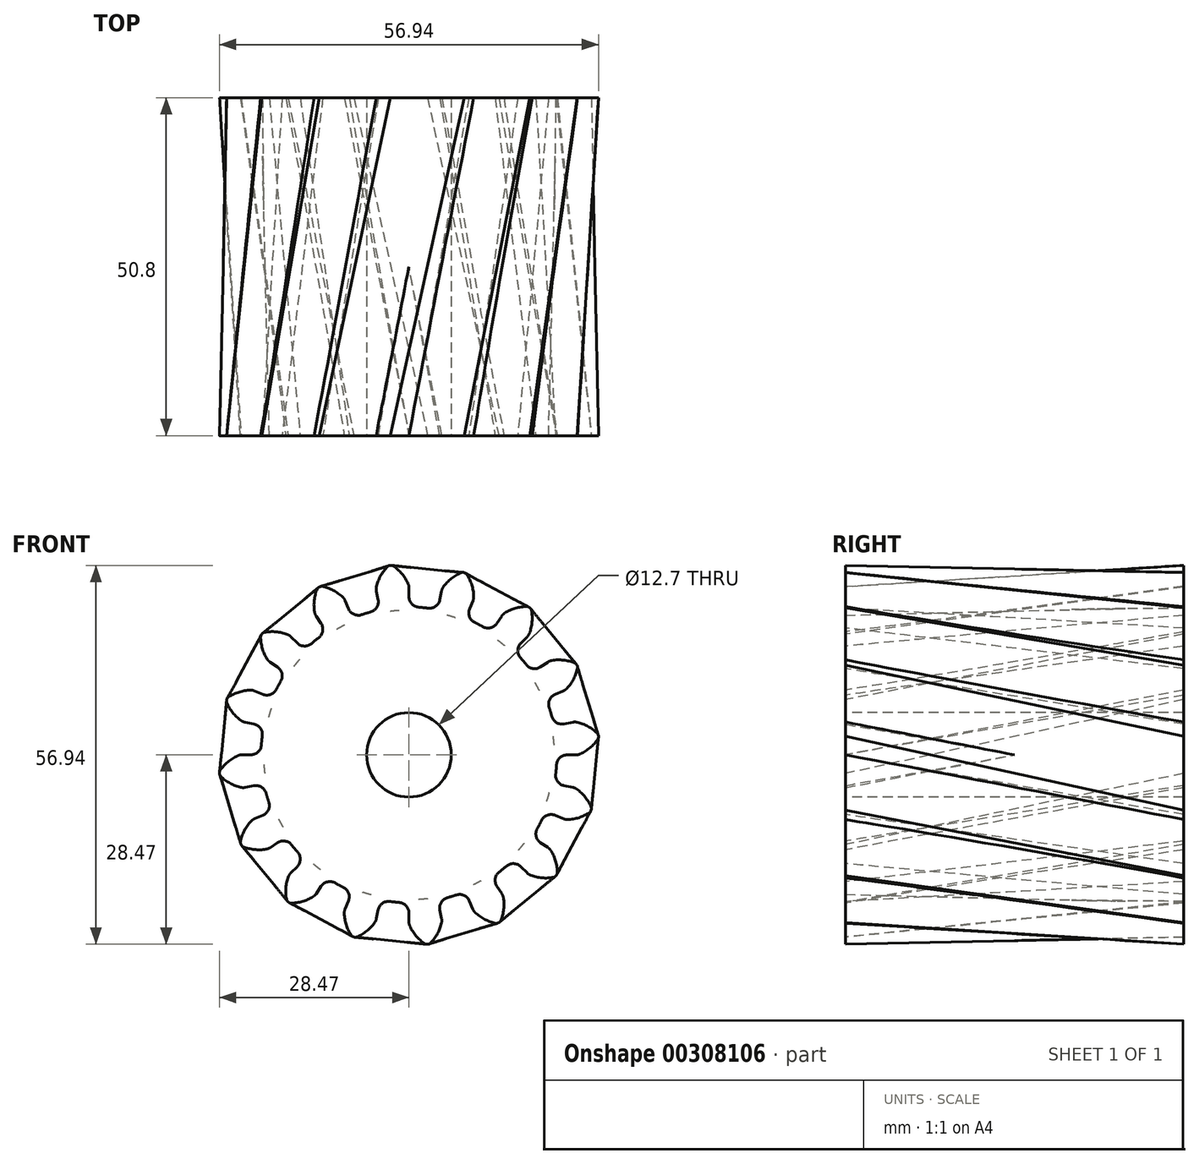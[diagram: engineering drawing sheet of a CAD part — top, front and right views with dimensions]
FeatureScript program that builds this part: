
annotation { "Feature Type Name" : "Feature", "Feature Type Description" : "" }
export const myFeature = defineFeature(function(context is Context, id is Id, definition is map)
    precondition{}
    {
        {
            var Q0;
            Q0=qCreatedBy(makeId("Front.planeOp"),FACE);
            var sketch = newSketch(context, id + "F0", { "sketchPlane" : qUnion([Q0])});
            skArc(sketch, "E0", {"start": v(-5.78, 21.46) * mm, "mid": v(-6.45, 21.27) * mm, "end": v(-7.11, 21.06) * mm});
            skArc(sketch, "E1.trimOffspring", {"start": v(-0.14, 25.74) * mm, "mid": v(-1.06, 27.21) * mm, "end": v(-2.36, 28.38) * mm});
            skLineSegment(sketch, "E2", {"start": v(-2.64, 28.47) * mm, "end": v(-2.8, 28.47) * mm});
            skLineSegment(sketch, "E3", {"start": v(0, 25.08) * mm, "end": v(0, 23.76) * mm});
            skLineSegment(sketch, "E4.MirrorCS", {"start": v(-2.96, 28.44) * mm, "end": v(-2.8, 28.47) * mm});
            skArc(sketch, "E5.MirrorCS", {"start": v(-4.89, 25.27) * mm, "mid": v(-4.27, 26.9) * mm, "end": v(-3.22, 28.3) * mm});
            skLineSegment(sketch, "E6.MirrorCS", {"start": v(-4.9, 24.6) * mm, "end": v(-4.64, 23.3) * mm});
            skPoint(sketch, "E7.orphan", {"position": v(-4.19, 21.03) * mm});
            skPoint(sketch, "E8.orphan", {"position": v(0, 21.44) * mm});
            skPoint(sketch, "E9.visualSharp", {"position": v(-3.1, 28.4) * mm});
            skArc(sketch, "E9.filletArc", {"start": v(-2.96, 28.44) * mm, "mid": v(-3.1, 28.38) * mm, "end": v(-3.22, 28.3) * mm});
            skPoint(sketch, "E10.visualSharp", {"position": v(-2.5, 28.47) * mm});
            skArc(sketch, "E10.filletArc", {"start": v(-2.36, 28.38) * mm, "mid": v(-2.5, 28.44) * mm, "end": v(-2.64, 28.47) * mm});
            skPoint(sketch, "E11.visualSharp", {"position": v(-4.96, 24.91) * mm});
            skArc(sketch, "E11.filletArc", {"start": v(-4.89, 25.27) * mm, "mid": v(-4.93, 24.94) * mm, "end": v(-4.9, 24.6) * mm});
            skPoint(sketch, "E12.visualSharp", {"position": v(0, 25.4) * mm});
            skArc(sketch, "E12.filletArc", {"start": v(0, 25.08) * mm, "mid": v(-0.03, 25.42) * mm, "end": v(-0.14, 25.74) * mm});
            skPoint(sketch, "E13.visualSharp", {"position": v(-4.34, 21.8) * mm});
            skArc(sketch, "E13.filletArc", {"start": v(-5.78, 21.46) * mm, "mid": v(-4.85, 22.15) * mm, "end": v(-4.64, 23.3) * mm});
            skPoint(sketch, "E14.visualSharp", {"position": v(0, 22.22) * mm});
            skArc(sketch, "E14.filletArc", {"start": v(0, 23.76) * mm, "mid": v(0.43, 22.67) * mm, "end": v(1.49, 22.18) * mm});
            skArc(sketch, "E15.1.0", {"start": v(-13.56, 17.61) * mm, "mid": v(-12.96, 18.61) * mm, "end": v(-13.2, 19.75) * mm});
            skLineSegment(sketch, "E15.1.1", {"start": v(-13.94, 20.85) * mm, "end": v(-13.2, 19.75) * mm});
            skArc(sketch, "E15.1.2", {"start": v(-14.19, 21.47) * mm, "mid": v(-14.1, 21.15) * mm, "end": v(-13.94, 20.85) * mm});
            skArc(sketch, "E15.1.3", {"start": v(-14.19, 21.47) * mm, "mid": v(-14.23, 23.22) * mm, "end": v(-13.8, 24.9) * mm});
            skArc(sketch, "E15.1.4", {"start": v(-13.62, 25.14) * mm, "mid": v(-13.73, 25.04) * mm, "end": v(-13.8, 24.9) * mm});
            skLineSegment(sketch, "E15.1.5", {"start": v(-13.62, 25.14) * mm, "end": v(-13.48, 25.23) * mm});
            skLineSegment(sketch, "E15.1.6", {"start": v(-13.34, 25.29) * mm, "end": v(-13.48, 25.23) * mm});
            skArc(sketch, "E15.1.7", {"start": v(-13.04, 25.32) * mm, "mid": v(-13.2, 25.32) * mm, "end": v(-13.34, 25.29) * mm});
            skArc(sketch, "E15.1.8", {"start": v(-9.97, 23.73) * mm, "mid": v(-11.4, 24.73) * mm, "end": v(-13.04, 25.32) * mm});
            skArc(sketch, "E15.1.9", {"start": v(-9.6, 23.18) * mm, "mid": v(-9.75, 23.47) * mm, "end": v(-9.97, 23.73) * mm});
            skLineSegment(sketch, "E15.1.10", {"start": v(-9.6, 23.18) * mm, "end": v(-9.09, 21.95) * mm});
            skArc(sketch, "E15.1.11", {"start": v(-9.09, 21.95) * mm, "mid": v(-8.28, 21.11) * mm, "end": v(-7.11, 21.06) * mm});
            skArc(sketch, "E15.2.0", {"start": v(-19.26, 11.08) * mm, "mid": v(-19.1, 12.24) * mm, "end": v(-19.76, 13.2) * mm});
            skLineSegment(sketch, "E15.2.1", {"start": v(-20.86, 13.93) * mm, "end": v(-19.76, 13.2) * mm});
            skArc(sketch, "E15.2.2", {"start": v(-21.32, 14.41) * mm, "mid": v(-21.12, 14.15) * mm, "end": v(-20.86, 13.93) * mm});
            skArc(sketch, "E15.2.3", {"start": v(-21.32, 14.41) * mm, "mid": v(-22.03, 16) * mm, "end": v(-22.29, 17.73) * mm});
            skArc(sketch, "E15.2.4", {"start": v(-22.2, 18.01) * mm, "mid": v(-22.26, 17.88) * mm, "end": v(-22.29, 17.73) * mm});
            skLineSegment(sketch, "E15.2.5", {"start": v(-22.2, 18.01) * mm, "end": v(-22.11, 18.15) * mm});
            skLineSegment(sketch, "E15.2.6", {"start": v(-22, 18.26) * mm, "end": v(-22.11, 18.15) * mm});
            skArc(sketch, "E15.2.7", {"start": v(-21.74, 18.4) * mm, "mid": v(-21.88, 18.35) * mm, "end": v(-22, 18.26) * mm});
            skArc(sketch, "E15.2.8", {"start": v(-18.3, 18.1) * mm, "mid": v(-20, 18.49) * mm, "end": v(-21.74, 18.4) * mm});
            skArc(sketch, "E15.2.9", {"start": v(-17.73, 17.74) * mm, "mid": v(-18, 17.95) * mm, "end": v(-18.3, 18.1) * mm});
            skLineSegment(sketch, "E15.2.10", {"start": v(-17.73, 17.74) * mm, "end": v(-16.8, 16.8) * mm});
            skArc(sketch, "E15.2.11", {"start": v(-16.8, 16.8) * mm, "mid": v(-15.73, 16.34) * mm, "end": v(-14.63, 16.73) * mm});
            skArc(sketch, "E15.3.0", {"start": v(-22.04, 2.87) * mm, "mid": v(-22.32, 4) * mm, "end": v(-23.3, 4.63) * mm});
            skLineSegment(sketch, "E15.3.1", {"start": v(-24.6, 4.89) * mm, "end": v(-23.3, 4.63) * mm});
            skArc(sketch, "E15.3.2", {"start": v(-25.22, 5.15) * mm, "mid": v(-24.92, 4.99) * mm, "end": v(-24.6, 4.89) * mm});
            skArc(sketch, "E15.3.3", {"start": v(-25.22, 5.15) * mm, "mid": v(-26.48, 6.35) * mm, "end": v(-27.37, 7.85) * mm});
            skArc(sketch, "E15.3.4", {"start": v(-27.4, 8.15) * mm, "mid": v(-27.41, 8) * mm, "end": v(-27.37, 7.85) * mm});
            skLineSegment(sketch, "E15.3.5", {"start": v(-27.4, 8.15) * mm, "end": v(-27.37, 8.3) * mm});
            skLineSegment(sketch, "E15.3.6", {"start": v(-27.31, 8.45) * mm, "end": v(-27.37, 8.3) * mm});
            skArc(sketch, "E15.3.7", {"start": v(-27.12, 8.68) * mm, "mid": v(-27.23, 8.58) * mm, "end": v(-27.31, 8.45) * mm});
            skArc(sketch, "E15.3.8", {"start": v(-23.83, 9.72) * mm, "mid": v(-25.55, 9.43) * mm, "end": v(-27.12, 8.68) * mm});
            skArc(sketch, "E15.3.9", {"start": v(-23.17, 9.6) * mm, "mid": v(-23.5, 9.7) * mm, "end": v(-23.83, 9.72) * mm});
            skLineSegment(sketch, "E15.3.10", {"start": v(-23.17, 9.6) * mm, "end": v(-21.95, 9.1) * mm});
            skArc(sketch, "E15.3.11", {"start": v(-21.95, 9.1) * mm, "mid": v(-20.78, 9.08) * mm, "end": v(-19.92, 9.86) * mm});
            skArc(sketch, "E15.4.0", {"start": v(-21.46, -5.78) * mm, "mid": v(-22.15, -4.85) * mm, "end": v(-23.3, -4.64) * mm});
            skLineSegment(sketch, "E15.4.1", {"start": v(-24.6, -4.9) * mm, "end": v(-23.3, -4.64) * mm});
            skArc(sketch, "E15.4.2", {"start": v(-25.27, -4.89) * mm, "mid": v(-24.94, -4.93) * mm, "end": v(-24.6, -4.9) * mm});
            skArc(sketch, "E15.4.3", {"start": v(-25.27, -4.89) * mm, "mid": v(-26.9, -4.27) * mm, "end": v(-28.3, -3.22) * mm});
            skArc(sketch, "E15.4.4", {"start": v(-28.44, -2.96) * mm, "mid": v(-28.38, -3.1) * mm, "end": v(-28.3, -3.22) * mm});
            skLineSegment(sketch, "E15.4.5", {"start": v(-28.44, -2.96) * mm, "end": v(-28.47, -2.8) * mm});
            skLineSegment(sketch, "E15.4.6", {"start": v(-28.47, -2.64) * mm, "end": v(-28.47, -2.8) * mm});
            skArc(sketch, "E15.4.7", {"start": v(-28.38, -2.36) * mm, "mid": v(-28.44, -2.5) * mm, "end": v(-28.47, -2.64) * mm});
            skArc(sketch, "E15.4.8", {"start": v(-25.74, -0.14) * mm, "mid": v(-27.21, -1.06) * mm, "end": v(-28.38, -2.36) * mm});
            skArc(sketch, "E15.4.9", {"start": v(-25.08, 0) * mm, "mid": v(-25.42, -0.03) * mm, "end": v(-25.74, -0.14) * mm});
            skLineSegment(sketch, "E15.4.10", {"start": v(-25.08, 0) * mm, "end": v(-23.76, 0) * mm});
            skArc(sketch, "E15.4.11", {"start": v(-23.76, 0) * mm, "mid": v(-22.67, 0.43) * mm, "end": v(-22.18, 1.49) * mm});
            skArc(sketch, "E15.5.0", {"start": v(-17.61, -13.56) * mm, "mid": v(-18.61, -12.96) * mm, "end": v(-19.75, -13.2) * mm});
            skLineSegment(sketch, "E15.5.1", {"start": v(-20.85, -13.94) * mm, "end": v(-19.75, -13.2) * mm});
            skArc(sketch, "E15.5.2", {"start": v(-21.47, -14.19) * mm, "mid": v(-21.15, -14.1) * mm, "end": v(-20.85, -13.94) * mm});
            skArc(sketch, "E15.5.3", {"start": v(-21.47, -14.19) * mm, "mid": v(-23.22, -14.23) * mm, "end": v(-24.9, -13.8) * mm});
            skArc(sketch, "E15.5.4", {"start": v(-25.14, -13.62) * mm, "mid": v(-25.04, -13.73) * mm, "end": v(-24.9, -13.8) * mm});
            skLineSegment(sketch, "E15.5.5", {"start": v(-25.14, -13.62) * mm, "end": v(-25.23, -13.48) * mm});
            skLineSegment(sketch, "E15.5.6", {"start": v(-25.29, -13.34) * mm, "end": v(-25.23, -13.48) * mm});
            skArc(sketch, "E15.5.7", {"start": v(-25.32, -13.04) * mm, "mid": v(-25.32, -13.2) * mm, "end": v(-25.29, -13.34) * mm});
            skArc(sketch, "E15.5.8", {"start": v(-23.73, -9.97) * mm, "mid": v(-24.73, -11.4) * mm, "end": v(-25.32, -13.04) * mm});
            skArc(sketch, "E15.5.9", {"start": v(-23.18, -9.6) * mm, "mid": v(-23.47, -9.75) * mm, "end": v(-23.73, -9.97) * mm});
            skLineSegment(sketch, "E15.5.10", {"start": v(-23.18, -9.6) * mm, "end": v(-21.95, -9.09) * mm});
            skArc(sketch, "E15.5.11", {"start": v(-21.95, -9.09) * mm, "mid": v(-21.11, -8.28) * mm, "end": v(-21.06, -7.11) * mm});
            skArc(sketch, "E15.6.0", {"start": v(-11.08, -19.26) * mm, "mid": v(-12.24, -19.1) * mm, "end": v(-13.2, -19.76) * mm});
            skLineSegment(sketch, "E15.6.1", {"start": v(-13.93, -20.86) * mm, "end": v(-13.2, -19.76) * mm});
            skArc(sketch, "E15.6.2", {"start": v(-14.41, -21.32) * mm, "mid": v(-14.15, -21.12) * mm, "end": v(-13.93, -20.86) * mm});
            skArc(sketch, "E15.6.3", {"start": v(-14.41, -21.32) * mm, "mid": v(-16, -22.03) * mm, "end": v(-17.73, -22.29) * mm});
            skArc(sketch, "E15.6.4", {"start": v(-18.01, -22.2) * mm, "mid": v(-17.88, -22.26) * mm, "end": v(-17.73, -22.29) * mm});
            skLineSegment(sketch, "E15.6.5", {"start": v(-18.01, -22.2) * mm, "end": v(-18.15, -22.11) * mm});
            skLineSegment(sketch, "E15.6.6", {"start": v(-18.26, -22) * mm, "end": v(-18.15, -22.11) * mm});
            skArc(sketch, "E15.6.7", {"start": v(-18.4, -21.74) * mm, "mid": v(-18.35, -21.88) * mm, "end": v(-18.26, -22) * mm});
            skArc(sketch, "E15.6.8", {"start": v(-18.1, -18.3) * mm, "mid": v(-18.49, -20) * mm, "end": v(-18.4, -21.74) * mm});
            skArc(sketch, "E15.6.9", {"start": v(-17.74, -17.73) * mm, "mid": v(-17.95, -18) * mm, "end": v(-18.1, -18.3) * mm});
            skLineSegment(sketch, "E15.6.10", {"start": v(-17.74, -17.73) * mm, "end": v(-16.8, -16.8) * mm});
            skArc(sketch, "E15.6.11", {"start": v(-16.8, -16.8) * mm, "mid": v(-16.34, -15.73) * mm, "end": v(-16.73, -14.63) * mm});
            skArc(sketch, "E15.7.0", {"start": v(-2.87, -22.04) * mm, "mid": v(-4, -22.32) * mm, "end": v(-4.63, -23.3) * mm});
            skLineSegment(sketch, "E15.7.1", {"start": v(-4.89, -24.6) * mm, "end": v(-4.63, -23.3) * mm});
            skArc(sketch, "E15.7.2", {"start": v(-5.15, -25.22) * mm, "mid": v(-4.99, -24.92) * mm, "end": v(-4.89, -24.6) * mm});
            skArc(sketch, "E15.7.3", {"start": v(-5.15, -25.22) * mm, "mid": v(-6.35, -26.48) * mm, "end": v(-7.85, -27.37) * mm});
            skArc(sketch, "E15.7.4", {"start": v(-8.15, -27.4) * mm, "mid": v(-8, -27.41) * mm, "end": v(-7.85, -27.37) * mm});
            skLineSegment(sketch, "E15.7.5", {"start": v(-8.15, -27.4) * mm, "end": v(-8.3, -27.37) * mm});
            skLineSegment(sketch, "E15.7.6", {"start": v(-8.45, -27.31) * mm, "end": v(-8.3, -27.37) * mm});
            skArc(sketch, "E15.7.7", {"start": v(-8.68, -27.12) * mm, "mid": v(-8.58, -27.23) * mm, "end": v(-8.45, -27.31) * mm});
            skArc(sketch, "E15.7.8", {"start": v(-9.72, -23.83) * mm, "mid": v(-9.43, -25.55) * mm, "end": v(-8.68, -27.12) * mm});
            skArc(sketch, "E15.7.9", {"start": v(-9.6, -23.17) * mm, "mid": v(-9.7, -23.5) * mm, "end": v(-9.72, -23.83) * mm});
            skLineSegment(sketch, "E15.7.10", {"start": v(-9.6, -23.17) * mm, "end": v(-9.1, -21.95) * mm});
            skArc(sketch, "E15.7.11", {"start": v(-9.1, -21.95) * mm, "mid": v(-9.08, -20.78) * mm, "end": v(-9.86, -19.92) * mm});
            skArc(sketch, "E15.8.0", {"start": v(5.78, -21.46) * mm, "mid": v(4.85, -22.15) * mm, "end": v(4.64, -23.3) * mm});
            skLineSegment(sketch, "E15.8.1", {"start": v(4.9, -24.6) * mm, "end": v(4.64, -23.3) * mm});
            skArc(sketch, "E15.8.2", {"start": v(4.89, -25.27) * mm, "mid": v(4.93, -24.94) * mm, "end": v(4.9, -24.6) * mm});
            skArc(sketch, "E15.8.3", {"start": v(4.89, -25.27) * mm, "mid": v(4.27, -26.9) * mm, "end": v(3.22, -28.3) * mm});
            skArc(sketch, "E15.8.4", {"start": v(2.96, -28.44) * mm, "mid": v(3.1, -28.38) * mm, "end": v(3.22, -28.3) * mm});
            skLineSegment(sketch, "E15.8.5", {"start": v(2.96, -28.44) * mm, "end": v(2.8, -28.47) * mm});
            skLineSegment(sketch, "E15.8.6", {"start": v(2.64, -28.47) * mm, "end": v(2.8, -28.47) * mm});
            skArc(sketch, "E15.8.7", {"start": v(2.36, -28.38) * mm, "mid": v(2.5, -28.44) * mm, "end": v(2.64, -28.47) * mm});
            skArc(sketch, "E15.8.8", {"start": v(0.14, -25.74) * mm, "mid": v(1.06, -27.21) * mm, "end": v(2.36, -28.38) * mm});
            skArc(sketch, "E15.8.9", {"start": v(0, -25.08) * mm, "mid": v(0.03, -25.42) * mm, "end": v(0.14, -25.74) * mm});
            skLineSegment(sketch, "E15.8.10", {"start": v(0, -25.08) * mm, "end": v(0, -23.76) * mm});
            skArc(sketch, "E15.8.11", {"start": v(0, -23.76) * mm, "mid": v(-0.43, -22.67) * mm, "end": v(-1.49, -22.18) * mm});
            skArc(sketch, "E15.9.0", {"start": v(13.56, -17.61) * mm, "mid": v(12.96, -18.61) * mm, "end": v(13.2, -19.75) * mm});
            skLineSegment(sketch, "E15.9.1", {"start": v(13.94, -20.85) * mm, "end": v(13.2, -19.75) * mm});
            skArc(sketch, "E15.9.2", {"start": v(14.19, -21.47) * mm, "mid": v(14.1, -21.15) * mm, "end": v(13.94, -20.85) * mm});
            skArc(sketch, "E15.9.3", {"start": v(14.19, -21.47) * mm, "mid": v(14.23, -23.22) * mm, "end": v(13.8, -24.9) * mm});
            skArc(sketch, "E15.9.4", {"start": v(13.62, -25.14) * mm, "mid": v(13.73, -25.04) * mm, "end": v(13.8, -24.9) * mm});
            skLineSegment(sketch, "E15.9.5", {"start": v(13.62, -25.14) * mm, "end": v(13.48, -25.23) * mm});
            skLineSegment(sketch, "E15.9.6", {"start": v(13.34, -25.29) * mm, "end": v(13.48, -25.23) * mm});
            skArc(sketch, "E15.9.7", {"start": v(13.04, -25.32) * mm, "mid": v(13.2, -25.32) * mm, "end": v(13.34, -25.29) * mm});
            skArc(sketch, "E15.9.8", {"start": v(9.97, -23.73) * mm, "mid": v(11.4, -24.73) * mm, "end": v(13.04, -25.32) * mm});
            skArc(sketch, "E15.9.9", {"start": v(9.6, -23.18) * mm, "mid": v(9.75, -23.47) * mm, "end": v(9.97, -23.73) * mm});
            skLineSegment(sketch, "E15.9.10", {"start": v(9.6, -23.18) * mm, "end": v(9.09, -21.95) * mm});
            skArc(sketch, "E15.9.11", {"start": v(9.09, -21.95) * mm, "mid": v(8.28, -21.11) * mm, "end": v(7.11, -21.06) * mm});
            skArc(sketch, "E15.10.0", {"start": v(19.26, -11.08) * mm, "mid": v(19.1, -12.24) * mm, "end": v(19.76, -13.2) * mm});
            skLineSegment(sketch, "E15.10.1", {"start": v(20.86, -13.93) * mm, "end": v(19.76, -13.2) * mm});
            skArc(sketch, "E15.10.2", {"start": v(21.32, -14.41) * mm, "mid": v(21.12, -14.15) * mm, "end": v(20.86, -13.93) * mm});
            skArc(sketch, "E15.10.3", {"start": v(21.32, -14.41) * mm, "mid": v(22.03, -16) * mm, "end": v(22.29, -17.73) * mm});
            skArc(sketch, "E15.10.4", {"start": v(22.2, -18.01) * mm, "mid": v(22.26, -17.88) * mm, "end": v(22.29, -17.73) * mm});
            skLineSegment(sketch, "E15.10.5", {"start": v(22.2, -18.01) * mm, "end": v(22.11, -18.15) * mm});
            skLineSegment(sketch, "E15.10.6", {"start": v(22, -18.26) * mm, "end": v(22.11, -18.15) * mm});
            skArc(sketch, "E15.10.7", {"start": v(21.74, -18.4) * mm, "mid": v(21.88, -18.35) * mm, "end": v(22, -18.26) * mm});
            skArc(sketch, "E15.10.8", {"start": v(18.3, -18.1) * mm, "mid": v(20, -18.49) * mm, "end": v(21.74, -18.4) * mm});
            skArc(sketch, "E15.10.9", {"start": v(17.73, -17.74) * mm, "mid": v(18, -17.95) * mm, "end": v(18.3, -18.1) * mm});
            skLineSegment(sketch, "E15.10.10", {"start": v(17.73, -17.74) * mm, "end": v(16.8, -16.8) * mm});
            skArc(sketch, "E15.10.11", {"start": v(16.8, -16.8) * mm, "mid": v(15.73, -16.34) * mm, "end": v(14.63, -16.73) * mm});
            skArc(sketch, "E15.11.0", {"start": v(22.04, -2.87) * mm, "mid": v(22.32, -4) * mm, "end": v(23.3, -4.63) * mm});
            skLineSegment(sketch, "E15.11.1", {"start": v(24.6, -4.89) * mm, "end": v(23.3, -4.63) * mm});
            skArc(sketch, "E15.11.2", {"start": v(25.22, -5.15) * mm, "mid": v(24.92, -4.99) * mm, "end": v(24.6, -4.89) * mm});
            skArc(sketch, "E15.11.3", {"start": v(25.22, -5.15) * mm, "mid": v(26.48, -6.35) * mm, "end": v(27.37, -7.85) * mm});
            skArc(sketch, "E15.11.4", {"start": v(27.4, -8.15) * mm, "mid": v(27.41, -8) * mm, "end": v(27.37, -7.85) * mm});
            skLineSegment(sketch, "E15.11.5", {"start": v(27.4, -8.15) * mm, "end": v(27.37, -8.3) * mm});
            skLineSegment(sketch, "E15.11.6", {"start": v(27.31, -8.45) * mm, "end": v(27.37, -8.3) * mm});
            skArc(sketch, "E15.11.7", {"start": v(27.12, -8.68) * mm, "mid": v(27.23, -8.58) * mm, "end": v(27.31, -8.45) * mm});
            skArc(sketch, "E15.11.8", {"start": v(23.83, -9.72) * mm, "mid": v(25.55, -9.43) * mm, "end": v(27.12, -8.68) * mm});
            skArc(sketch, "E15.11.9", {"start": v(23.17, -9.6) * mm, "mid": v(23.5, -9.7) * mm, "end": v(23.83, -9.72) * mm});
            skLineSegment(sketch, "E15.11.10", {"start": v(23.17, -9.6) * mm, "end": v(21.95, -9.1) * mm});
            skArc(sketch, "E15.11.11", {"start": v(21.95, -9.1) * mm, "mid": v(20.78, -9.08) * mm, "end": v(19.92, -9.86) * mm});
            skArc(sketch, "E15.12.0", {"start": v(21.46, 5.78) * mm, "mid": v(22.15, 4.85) * mm, "end": v(23.3, 4.64) * mm});
            skLineSegment(sketch, "E15.12.1", {"start": v(24.6, 4.9) * mm, "end": v(23.3, 4.64) * mm});
            skArc(sketch, "E15.12.2", {"start": v(25.27, 4.89) * mm, "mid": v(24.94, 4.93) * mm, "end": v(24.6, 4.9) * mm});
            skArc(sketch, "E15.12.3", {"start": v(25.27, 4.89) * mm, "mid": v(26.9, 4.27) * mm, "end": v(28.3, 3.22) * mm});
            skArc(sketch, "E15.12.4", {"start": v(28.44, 2.96) * mm, "mid": v(28.38, 3.1) * mm, "end": v(28.3, 3.22) * mm});
            skLineSegment(sketch, "E15.12.5", {"start": v(28.44, 2.96) * mm, "end": v(28.47, 2.8) * mm});
            skLineSegment(sketch, "E15.12.6", {"start": v(28.47, 2.64) * mm, "end": v(28.47, 2.8) * mm});
            skArc(sketch, "E15.12.7", {"start": v(28.38, 2.36) * mm, "mid": v(28.44, 2.5) * mm, "end": v(28.47, 2.64) * mm});
            skArc(sketch, "E15.12.8", {"start": v(25.74, 0.14) * mm, "mid": v(27.21, 1.06) * mm, "end": v(28.38, 2.36) * mm});
            skArc(sketch, "E15.12.9", {"start": v(25.08, 0) * mm, "mid": v(25.42, 0.03) * mm, "end": v(25.74, 0.14) * mm});
            skLineSegment(sketch, "E15.12.10", {"start": v(25.08, 0) * mm, "end": v(23.76, 0) * mm});
            skArc(sketch, "E15.12.11", {"start": v(23.76, 0) * mm, "mid": v(22.67, -0.43) * mm, "end": v(22.18, -1.49) * mm});
            skArc(sketch, "E15.13.0", {"start": v(17.61, 13.56) * mm, "mid": v(18.61, 12.96) * mm, "end": v(19.75, 13.2) * mm});
            skLineSegment(sketch, "E15.13.1", {"start": v(20.85, 13.94) * mm, "end": v(19.75, 13.2) * mm});
            skArc(sketch, "E15.13.2", {"start": v(21.47, 14.19) * mm, "mid": v(21.15, 14.1) * mm, "end": v(20.85, 13.94) * mm});
            skArc(sketch, "E15.13.3", {"start": v(21.47, 14.19) * mm, "mid": v(23.22, 14.23) * mm, "end": v(24.9, 13.8) * mm});
            skArc(sketch, "E15.13.4", {"start": v(25.14, 13.62) * mm, "mid": v(25.04, 13.73) * mm, "end": v(24.9, 13.8) * mm});
            skLineSegment(sketch, "E15.13.5", {"start": v(25.14, 13.62) * mm, "end": v(25.23, 13.48) * mm});
            skLineSegment(sketch, "E15.13.6", {"start": v(25.29, 13.34) * mm, "end": v(25.23, 13.48) * mm});
            skArc(sketch, "E15.13.7", {"start": v(25.32, 13.04) * mm, "mid": v(25.32, 13.2) * mm, "end": v(25.29, 13.34) * mm});
            skArc(sketch, "E15.13.8", {"start": v(23.73, 9.97) * mm, "mid": v(24.73, 11.4) * mm, "end": v(25.32, 13.04) * mm});
            skArc(sketch, "E15.13.9", {"start": v(23.18, 9.6) * mm, "mid": v(23.47, 9.75) * mm, "end": v(23.73, 9.97) * mm});
            skLineSegment(sketch, "E15.13.10", {"start": v(23.18, 9.6) * mm, "end": v(21.95, 9.09) * mm});
            skArc(sketch, "E15.13.11", {"start": v(21.95, 9.09) * mm, "mid": v(21.11, 8.28) * mm, "end": v(21.06, 7.11) * mm});
            skArc(sketch, "E15.14.0", {"start": v(11.08, 19.26) * mm, "mid": v(12.24, 19.1) * mm, "end": v(13.2, 19.76) * mm});
            skLineSegment(sketch, "E15.14.1", {"start": v(13.93, 20.86) * mm, "end": v(13.2, 19.76) * mm});
            skArc(sketch, "E15.14.2", {"start": v(14.41, 21.32) * mm, "mid": v(14.15, 21.12) * mm, "end": v(13.93, 20.86) * mm});
            skArc(sketch, "E15.14.3", {"start": v(14.41, 21.32) * mm, "mid": v(16, 22.03) * mm, "end": v(17.73, 22.29) * mm});
            skArc(sketch, "E15.14.4", {"start": v(18.01, 22.2) * mm, "mid": v(17.88, 22.26) * mm, "end": v(17.73, 22.29) * mm});
            skLineSegment(sketch, "E15.14.5", {"start": v(18.01, 22.2) * mm, "end": v(18.15, 22.11) * mm});
            skLineSegment(sketch, "E15.14.6", {"start": v(18.26, 22) * mm, "end": v(18.15, 22.11) * mm});
            skArc(sketch, "E15.14.7", {"start": v(18.4, 21.74) * mm, "mid": v(18.35, 21.88) * mm, "end": v(18.26, 22) * mm});
            skArc(sketch, "E15.14.8", {"start": v(18.1, 18.3) * mm, "mid": v(18.49, 20) * mm, "end": v(18.4, 21.74) * mm});
            skArc(sketch, "E15.14.9", {"start": v(17.74, 17.73) * mm, "mid": v(17.95, 18) * mm, "end": v(18.1, 18.3) * mm});
            skLineSegment(sketch, "E15.14.10", {"start": v(17.74, 17.73) * mm, "end": v(16.8, 16.8) * mm});
            skArc(sketch, "E15.14.11", {"start": v(16.8, 16.8) * mm, "mid": v(16.34, 15.73) * mm, "end": v(16.73, 14.63) * mm});
            skArc(sketch, "E15.15.0", {"start": v(2.87, 22.04) * mm, "mid": v(4, 22.32) * mm, "end": v(4.63, 23.3) * mm});
            skLineSegment(sketch, "E15.15.1", {"start": v(4.89, 24.6) * mm, "end": v(4.63, 23.3) * mm});
            skArc(sketch, "E15.15.2", {"start": v(5.15, 25.22) * mm, "mid": v(4.99, 24.92) * mm, "end": v(4.89, 24.6) * mm});
            skArc(sketch, "E15.15.3", {"start": v(5.15, 25.22) * mm, "mid": v(6.35, 26.48) * mm, "end": v(7.85, 27.37) * mm});
            skArc(sketch, "E15.15.4", {"start": v(8.15, 27.4) * mm, "mid": v(8, 27.41) * mm, "end": v(7.85, 27.37) * mm});
            skLineSegment(sketch, "E15.15.5", {"start": v(8.15, 27.4) * mm, "end": v(8.3, 27.37) * mm});
            skLineSegment(sketch, "E15.15.6", {"start": v(8.45, 27.31) * mm, "end": v(8.3, 27.37) * mm});
            skArc(sketch, "E15.15.7", {"start": v(8.68, 27.12) * mm, "mid": v(8.58, 27.23) * mm, "end": v(8.45, 27.31) * mm});
            skArc(sketch, "E15.15.8", {"start": v(9.72, 23.83) * mm, "mid": v(9.43, 25.55) * mm, "end": v(8.68, 27.12) * mm});
            skArc(sketch, "E15.15.9", {"start": v(9.6, 23.17) * mm, "mid": v(9.7, 23.5) * mm, "end": v(9.72, 23.83) * mm});
            skLineSegment(sketch, "E15.15.10", {"start": v(9.6, 23.17) * mm, "end": v(9.1, 21.95) * mm});
            skArc(sketch, "E15.15.11", {"start": v(9.1, 21.95) * mm, "mid": v(9.08, 20.78) * mm, "end": v(9.86, 19.92) * mm});
            skArc(sketch, "E16.trimOffspring", {"start": v(-17.61, -13.56) * mm, "mid": v(-17.18, -14.1) * mm, "end": v(-16.73, -14.63) * mm});
            skArc(sketch, "E17.trimOffspring", {"start": v(-21.46, -5.78) * mm, "mid": v(-21.27, -6.45) * mm, "end": v(-21.06, -7.11) * mm});
            skArc(sketch, "E18.trimOffspring", {"start": v(-22.04, 2.87) * mm, "mid": v(-22.12, 2.18) * mm, "end": v(-22.18, 1.49) * mm});
            skArc(sketch, "E19.trimOffspring", {"start": v(-19.26, 11.08) * mm, "mid": v(-19.6, 10.48) * mm, "end": v(-19.92, 9.86) * mm});
            skArc(sketch, "E20.trimOffspring", {"start": v(-13.56, 17.61) * mm, "mid": v(-14.1, 17.18) * mm, "end": v(-14.63, 16.73) * mm});
            skArc(sketch, "E21.trimOffspring", {"start": v(2.87, 22.04) * mm, "mid": v(2.18, 22.12) * mm, "end": v(1.49, 22.18) * mm});
            skArc(sketch, "E22.trimOffspring", {"start": v(11.08, 19.26) * mm, "mid": v(10.48, 19.6) * mm, "end": v(9.86, 19.92) * mm});
            skArc(sketch, "E23.trimOffspring", {"start": v(17.61, 13.56) * mm, "mid": v(17.18, 14.1) * mm, "end": v(16.73, 14.63) * mm});
            skArc(sketch, "E24.trimOffspring", {"start": v(21.46, 5.78) * mm, "mid": v(21.27, 6.45) * mm, "end": v(21.06, 7.11) * mm});
            skArc(sketch, "E25.trimOffspring", {"start": v(22.04, -2.87) * mm, "mid": v(22.12, -2.18) * mm, "end": v(22.18, -1.49) * mm});
            skArc(sketch, "E26.trimOffspring", {"start": v(-2.87, -22.04) * mm, "mid": v(-2.18, -22.12) * mm, "end": v(-1.49, -22.18) * mm});
            skArc(sketch, "E27.trimOffspring", {"start": v(-11.08, -19.26) * mm, "mid": v(-10.48, -19.6) * mm, "end": v(-9.86, -19.92) * mm});
            skArc(sketch, "E28.trimOffspring", {"start": v(5.78, -21.46) * mm, "mid": v(6.45, -21.27) * mm, "end": v(7.11, -21.06) * mm});
            skArc(sketch, "E29.trimOffspring", {"start": v(13.56, -17.61) * mm, "mid": v(14.1, -17.18) * mm, "end": v(14.63, -16.73) * mm});
            skArc(sketch, "E30.trimOffspring", {"start": v(19.26, -11.08) * mm, "mid": v(19.6, -10.48) * mm, "end": v(19.92, -9.86) * mm});
            skSolve(sketch);
        }
        {
            var Q0;
            Q0=makeQuery(id+"F0.imprint","IMPRINT",FACE,{"disambiguationData":[TD([[makeQuery(id+"F0.imprint","IMPRINT",EDGE,{"derivedFrom":sQuery(id+"F0.wireOp",EDGE,"E0")}),1.0]])]});
            cPlane(context, id + "F1", {"entities" : qUnion([Q0]), "cplaneType" : CPlaneType.OFFSET, "offset" : 50.8 * mm, "width" : 152.4 * mm, "height" : 152.4 * mm});
        }
        {
            var Q0;
            Q0=qCreatedBy(id+"F1.planeOp",FACE);
            var sketch = newSketch(context, id + "F2", { "sketchPlane" : qUnion([Q0])});
            skArc(sketch, "E31.0.0", {"start": v(-22.29, 17.73) * mm, "mid": v(-22.03, 16) * mm, "end": v(-21.32, 14.41) * mm});
            skArc(sketch, "E31.0.1", {"start": v(-21.32, 14.41) * mm, "mid": v(-21.12, 14.15) * mm, "end": v(-20.86, 13.93) * mm});
            skLineSegment(sketch, "E31.0.2", {"start": v(-20.86, 13.93) * mm, "end": v(-19.76, 13.2) * mm});
            skArc(sketch, "E31.0.3", {"start": v(-19.76, 13.2) * mm, "mid": v(-19.1, 12.24) * mm, "end": v(-19.26, 11.08) * mm});
            skArc(sketch, "E31.0.4", {"start": v(-19.26, 11.08) * mm, "mid": v(-19.6, 10.48) * mm, "end": v(-19.92, 9.86) * mm});
            skArc(sketch, "E31.0.5", {"start": v(-19.92, 9.86) * mm, "mid": v(-20.78, 9.08) * mm, "end": v(-21.95, 9.1) * mm});
            skLineSegment(sketch, "E31.0.6", {"start": v(-21.95, 9.1) * mm, "end": v(-23.17, 9.6) * mm});
            skArc(sketch, "E31.0.7", {"start": v(-23.17, 9.6) * mm, "mid": v(-23.5, 9.7) * mm, "end": v(-23.83, 9.72) * mm});
            skArc(sketch, "E31.0.8", {"start": v(-23.83, 9.72) * mm, "mid": v(-25.55, 9.43) * mm, "end": v(-27.12, 8.68) * mm});
            skArc(sketch, "E31.0.9", {"start": v(-27.12, 8.68) * mm, "mid": v(-27.23, 8.58) * mm, "end": v(-27.31, 8.45) * mm});
            skLineSegment(sketch, "E31.0.10", {"start": v(-27.31, 8.45) * mm, "end": v(-27.37, 8.3) * mm});
            skLineSegment(sketch, "E31.0.11", {"start": v(-27.37, 8.3) * mm, "end": v(-27.4, 8.15) * mm});
            skArc(sketch, "E31.0.12", {"start": v(-27.4, 8.15) * mm, "mid": v(-27.41, 8) * mm, "end": v(-27.37, 7.85) * mm});
            skArc(sketch, "E31.0.13", {"start": v(-27.37, 7.85) * mm, "mid": v(-26.48, 6.35) * mm, "end": v(-25.22, 5.15) * mm});
            skArc(sketch, "E31.0.14", {"start": v(-25.22, 5.15) * mm, "mid": v(-24.92, 4.99) * mm, "end": v(-24.6, 4.89) * mm});
            skLineSegment(sketch, "E31.0.15", {"start": v(-24.6, 4.89) * mm, "end": v(-23.3, 4.63) * mm});
            skArc(sketch, "E31.0.16", {"start": v(-23.3, 4.63) * mm, "mid": v(-22.32, 4) * mm, "end": v(-22.04, 2.87) * mm});
            skArc(sketch, "E31.0.17", {"start": v(-22.04, 2.87) * mm, "mid": v(-22.12, 2.18) * mm, "end": v(-22.18, 1.49) * mm});
            skArc(sketch, "E31.0.18", {"start": v(-22.18, 1.49) * mm, "mid": v(-22.67, 0.43) * mm, "end": v(-23.76, 0) * mm});
            skLineSegment(sketch, "E31.0.19", {"start": v(-23.76, 0) * mm, "end": v(-25.08, 0) * mm});
            skArc(sketch, "E31.0.20", {"start": v(-25.08, 0) * mm, "mid": v(-25.42, -0.03) * mm, "end": v(-25.74, -0.14) * mm});
            skArc(sketch, "E31.0.21", {"start": v(-25.74, -0.14) * mm, "mid": v(-27.21, -1.06) * mm, "end": v(-28.38, -2.36) * mm});
            skArc(sketch, "E31.0.22", {"start": v(-28.38, -2.36) * mm, "mid": v(-28.44, -2.5) * mm, "end": v(-28.47, -2.64) * mm});
            skLineSegment(sketch, "E31.0.23", {"start": v(-28.47, -2.64) * mm, "end": v(-28.47, -2.8) * mm});
            skLineSegment(sketch, "E31.0.24", {"start": v(-28.47, -2.8) * mm, "end": v(-28.44, -2.96) * mm});
            skArc(sketch, "E31.0.25", {"start": v(-28.44, -2.96) * mm, "mid": v(-28.38, -3.1) * mm, "end": v(-28.3, -3.22) * mm});
            skArc(sketch, "E31.0.26", {"start": v(-28.3, -3.22) * mm, "mid": v(-26.9, -4.27) * mm, "end": v(-25.27, -4.89) * mm});
            skArc(sketch, "E31.0.27", {"start": v(-25.27, -4.89) * mm, "mid": v(-24.94, -4.93) * mm, "end": v(-24.6, -4.9) * mm});
            skLineSegment(sketch, "E31.0.28", {"start": v(-24.6, -4.9) * mm, "end": v(-23.3, -4.64) * mm});
            skArc(sketch, "E31.0.29", {"start": v(-23.3, -4.64) * mm, "mid": v(-22.15, -4.85) * mm, "end": v(-21.46, -5.78) * mm});
            skArc(sketch, "E31.0.30", {"start": v(-21.46, -5.78) * mm, "mid": v(-21.27, -6.45) * mm, "end": v(-21.06, -7.11) * mm});
            skArc(sketch, "E31.0.31", {"start": v(-21.06, -7.11) * mm, "mid": v(-21.11, -8.28) * mm, "end": v(-21.95, -9.09) * mm});
            skLineSegment(sketch, "E31.0.32", {"start": v(-21.95, -9.09) * mm, "end": v(-23.18, -9.6) * mm});
            skArc(sketch, "E31.0.33", {"start": v(-23.18, -9.6) * mm, "mid": v(-23.47, -9.75) * mm, "end": v(-23.73, -9.97) * mm});
            skArc(sketch, "E31.0.34", {"start": v(-23.73, -9.97) * mm, "mid": v(-24.73, -11.4) * mm, "end": v(-25.32, -13.04) * mm});
            skArc(sketch, "E31.0.35", {"start": v(-25.32, -13.04) * mm, "mid": v(-25.32, -13.2) * mm, "end": v(-25.29, -13.34) * mm});
            skLineSegment(sketch, "E31.0.36", {"start": v(-25.29, -13.34) * mm, "end": v(-25.23, -13.48) * mm});
            skLineSegment(sketch, "E31.0.37", {"start": v(-25.23, -13.48) * mm, "end": v(-25.14, -13.62) * mm});
            skArc(sketch, "E31.0.38", {"start": v(-25.14, -13.62) * mm, "mid": v(-25.04, -13.73) * mm, "end": v(-24.9, -13.8) * mm});
            skArc(sketch, "E31.0.39", {"start": v(-24.9, -13.8) * mm, "mid": v(-23.22, -14.23) * mm, "end": v(-21.47, -14.19) * mm});
            skArc(sketch, "E31.0.40", {"start": v(-21.47, -14.19) * mm, "mid": v(-21.15, -14.1) * mm, "end": v(-20.85, -13.94) * mm});
            skLineSegment(sketch, "E31.0.41", {"start": v(-20.85, -13.94) * mm, "end": v(-19.75, -13.2) * mm});
            skArc(sketch, "E31.0.42", {"start": v(-19.75, -13.2) * mm, "mid": v(-18.61, -12.96) * mm, "end": v(-17.61, -13.56) * mm});
            skArc(sketch, "E31.0.43", {"start": v(-17.61, -13.56) * mm, "mid": v(-17.18, -14.1) * mm, "end": v(-16.73, -14.63) * mm});
            skArc(sketch, "E31.0.44", {"start": v(-16.73, -14.63) * mm, "mid": v(-16.34, -15.73) * mm, "end": v(-16.8, -16.8) * mm});
            skLineSegment(sketch, "E31.0.45", {"start": v(-16.8, -16.8) * mm, "end": v(-17.74, -17.73) * mm});
            skArc(sketch, "E31.0.46", {"start": v(-17.74, -17.73) * mm, "mid": v(-17.95, -18) * mm, "end": v(-18.1, -18.3) * mm});
            skArc(sketch, "E31.0.47", {"start": v(-18.1, -18.3) * mm, "mid": v(-18.49, -20) * mm, "end": v(-18.4, -21.74) * mm});
            skArc(sketch, "E31.0.48", {"start": v(-18.4, -21.74) * mm, "mid": v(-18.35, -21.88) * mm, "end": v(-18.26, -22) * mm});
            skLineSegment(sketch, "E31.0.49", {"start": v(-18.26, -22) * mm, "end": v(-18.15, -22.11) * mm});
            skLineSegment(sketch, "E31.0.50", {"start": v(-18.15, -22.11) * mm, "end": v(-18.01, -22.2) * mm});
            skArc(sketch, "E31.0.51", {"start": v(-18.01, -22.2) * mm, "mid": v(-17.88, -22.26) * mm, "end": v(-17.73, -22.29) * mm});
            skArc(sketch, "E31.0.52", {"start": v(-17.73, -22.29) * mm, "mid": v(-16, -22.03) * mm, "end": v(-14.41, -21.32) * mm});
            skArc(sketch, "E31.0.53", {"start": v(-14.41, -21.32) * mm, "mid": v(-14.15, -21.12) * mm, "end": v(-13.93, -20.86) * mm});
            skLineSegment(sketch, "E31.0.54", {"start": v(-13.93, -20.86) * mm, "end": v(-13.2, -19.76) * mm});
            skArc(sketch, "E31.0.55", {"start": v(-13.2, -19.76) * mm, "mid": v(-12.24, -19.1) * mm, "end": v(-11.08, -19.26) * mm});
            skArc(sketch, "E31.0.56", {"start": v(-11.08, -19.26) * mm, "mid": v(-10.48, -19.6) * mm, "end": v(-9.86, -19.92) * mm});
            skArc(sketch, "E31.0.57", {"start": v(-9.86, -19.92) * mm, "mid": v(-9.08, -20.78) * mm, "end": v(-9.1, -21.95) * mm});
            skLineSegment(sketch, "E31.0.58", {"start": v(-9.1, -21.95) * mm, "end": v(-9.6, -23.17) * mm});
            skArc(sketch, "E31.0.59", {"start": v(-9.6, -23.17) * mm, "mid": v(-9.7, -23.5) * mm, "end": v(-9.72, -23.83) * mm});
            skArc(sketch, "E31.0.60", {"start": v(-9.72, -23.83) * mm, "mid": v(-9.43, -25.55) * mm, "end": v(-8.68, -27.12) * mm});
            skArc(sketch, "E31.0.61", {"start": v(-8.68, -27.12) * mm, "mid": v(-8.58, -27.23) * mm, "end": v(-8.45, -27.31) * mm});
            skLineSegment(sketch, "E31.0.62", {"start": v(-8.45, -27.31) * mm, "end": v(-8.3, -27.37) * mm});
            skLineSegment(sketch, "E31.0.63", {"start": v(-8.3, -27.37) * mm, "end": v(-8.15, -27.4) * mm});
            skArc(sketch, "E31.0.64", {"start": v(-8.15, -27.4) * mm, "mid": v(-8, -27.41) * mm, "end": v(-7.85, -27.37) * mm});
            skArc(sketch, "E31.0.65", {"start": v(-7.85, -27.37) * mm, "mid": v(-6.35, -26.48) * mm, "end": v(-5.15, -25.22) * mm});
            skArc(sketch, "E31.0.66", {"start": v(-5.15, -25.22) * mm, "mid": v(-4.99, -24.92) * mm, "end": v(-4.89, -24.6) * mm});
            skLineSegment(sketch, "E31.0.67", {"start": v(-4.89, -24.6) * mm, "end": v(-4.63, -23.3) * mm});
            skArc(sketch, "E31.0.68", {"start": v(-4.63, -23.3) * mm, "mid": v(-4, -22.32) * mm, "end": v(-2.87, -22.04) * mm});
            skArc(sketch, "E31.0.69", {"start": v(-2.87, -22.04) * mm, "mid": v(-2.18, -22.12) * mm, "end": v(-1.49, -22.18) * mm});
            skArc(sketch, "E31.0.70", {"start": v(-1.49, -22.18) * mm, "mid": v(-0.43, -22.67) * mm, "end": v(0, -23.76) * mm});
            skLineSegment(sketch, "E31.0.71", {"start": v(0, -23.76) * mm, "end": v(0, -25.08) * mm});
            skArc(sketch, "E31.0.72", {"start": v(0, -25.08) * mm, "mid": v(0.03, -25.42) * mm, "end": v(0.14, -25.74) * mm});
            skArc(sketch, "E31.0.73", {"start": v(0.14, -25.74) * mm, "mid": v(1.06, -27.21) * mm, "end": v(2.36, -28.38) * mm});
            skArc(sketch, "E31.0.74", {"start": v(2.36, -28.38) * mm, "mid": v(2.5, -28.44) * mm, "end": v(2.64, -28.47) * mm});
            skLineSegment(sketch, "E31.0.75", {"start": v(2.64, -28.47) * mm, "end": v(2.8, -28.47) * mm});
            skLineSegment(sketch, "E31.0.76", {"start": v(2.8, -28.47) * mm, "end": v(2.96, -28.44) * mm});
            skArc(sketch, "E31.0.77", {"start": v(2.96, -28.44) * mm, "mid": v(3.1, -28.38) * mm, "end": v(3.22, -28.3) * mm});
            skArc(sketch, "E31.0.78", {"start": v(3.22, -28.3) * mm, "mid": v(4.27, -26.9) * mm, "end": v(4.89, -25.27) * mm});
            skArc(sketch, "E31.0.79", {"start": v(4.89, -25.27) * mm, "mid": v(4.93, -24.94) * mm, "end": v(4.9, -24.6) * mm});
            skLineSegment(sketch, "E31.0.80", {"start": v(4.9, -24.6) * mm, "end": v(4.64, -23.3) * mm});
            skArc(sketch, "E31.0.81", {"start": v(4.64, -23.3) * mm, "mid": v(4.85, -22.15) * mm, "end": v(5.78, -21.46) * mm});
            skArc(sketch, "E31.0.82", {"start": v(5.78, -21.46) * mm, "mid": v(6.45, -21.27) * mm, "end": v(7.11, -21.06) * mm});
            skArc(sketch, "E31.0.83", {"start": v(7.11, -21.06) * mm, "mid": v(8.28, -21.11) * mm, "end": v(9.09, -21.95) * mm});
            skLineSegment(sketch, "E31.0.84", {"start": v(9.09, -21.95) * mm, "end": v(9.6, -23.18) * mm});
            skArc(sketch, "E31.0.85", {"start": v(9.6, -23.18) * mm, "mid": v(9.75, -23.47) * mm, "end": v(9.97, -23.73) * mm});
            skArc(sketch, "E31.0.86", {"start": v(9.97, -23.73) * mm, "mid": v(11.4, -24.73) * mm, "end": v(13.04, -25.32) * mm});
            skArc(sketch, "E31.0.87", {"start": v(13.04, -25.32) * mm, "mid": v(13.2, -25.32) * mm, "end": v(13.34, -25.29) * mm});
            skLineSegment(sketch, "E31.0.88", {"start": v(13.34, -25.29) * mm, "end": v(13.48, -25.23) * mm});
            skLineSegment(sketch, "E31.0.89", {"start": v(13.48, -25.23) * mm, "end": v(13.62, -25.14) * mm});
            skArc(sketch, "E31.0.90", {"start": v(13.62, -25.14) * mm, "mid": v(13.73, -25.04) * mm, "end": v(13.8, -24.9) * mm});
            skArc(sketch, "E31.0.91", {"start": v(13.8, -24.9) * mm, "mid": v(14.23, -23.22) * mm, "end": v(14.19, -21.47) * mm});
            skArc(sketch, "E31.0.92", {"start": v(14.19, -21.47) * mm, "mid": v(14.1, -21.15) * mm, "end": v(13.94, -20.85) * mm});
            skLineSegment(sketch, "E31.0.93", {"start": v(13.94, -20.85) * mm, "end": v(13.2, -19.75) * mm});
            skArc(sketch, "E31.0.94", {"start": v(13.2, -19.75) * mm, "mid": v(12.96, -18.61) * mm, "end": v(13.56, -17.61) * mm});
            skArc(sketch, "E31.0.95", {"start": v(13.56, -17.61) * mm, "mid": v(14.1, -17.18) * mm, "end": v(14.63, -16.73) * mm});
            skArc(sketch, "E31.0.96", {"start": v(14.63, -16.73) * mm, "mid": v(15.73, -16.34) * mm, "end": v(16.8, -16.8) * mm});
            skLineSegment(sketch, "E31.0.97", {"start": v(16.8, -16.8) * mm, "end": v(17.73, -17.74) * mm});
            skArc(sketch, "E31.0.98", {"start": v(17.73, -17.74) * mm, "mid": v(18, -17.95) * mm, "end": v(18.3, -18.1) * mm});
            skArc(sketch, "E31.0.99", {"start": v(18.3, -18.1) * mm, "mid": v(20, -18.49) * mm, "end": v(21.74, -18.4) * mm});
            skArc(sketch, "E31.0.100", {"start": v(21.74, -18.4) * mm, "mid": v(21.88, -18.35) * mm, "end": v(22, -18.26) * mm});
            skLineSegment(sketch, "E31.0.101", {"start": v(22, -18.26) * mm, "end": v(22.11, -18.15) * mm});
            skLineSegment(sketch, "E31.0.102", {"start": v(22.11, -18.15) * mm, "end": v(22.2, -18.01) * mm});
            skArc(sketch, "E31.0.103", {"start": v(22.2, -18.01) * mm, "mid": v(22.26, -17.88) * mm, "end": v(22.29, -17.73) * mm});
            skArc(sketch, "E31.0.104", {"start": v(22.29, -17.73) * mm, "mid": v(22.03, -16) * mm, "end": v(21.32, -14.41) * mm});
            skArc(sketch, "E31.0.105", {"start": v(21.32, -14.41) * mm, "mid": v(21.12, -14.15) * mm, "end": v(20.86, -13.93) * mm});
            skLineSegment(sketch, "E31.0.106", {"start": v(20.86, -13.93) * mm, "end": v(19.76, -13.2) * mm});
            skArc(sketch, "E31.0.107", {"start": v(19.76, -13.2) * mm, "mid": v(19.1, -12.24) * mm, "end": v(19.26, -11.08) * mm});
            skArc(sketch, "E31.0.108", {"start": v(19.26, -11.08) * mm, "mid": v(19.6, -10.48) * mm, "end": v(19.92, -9.86) * mm});
            skArc(sketch, "E31.0.109", {"start": v(19.92, -9.86) * mm, "mid": v(20.78, -9.08) * mm, "end": v(21.95, -9.1) * mm});
            skLineSegment(sketch, "E31.0.110", {"start": v(21.95, -9.1) * mm, "end": v(23.17, -9.6) * mm});
            skArc(sketch, "E31.0.111", {"start": v(23.17, -9.6) * mm, "mid": v(23.5, -9.7) * mm, "end": v(23.83, -9.72) * mm});
            skArc(sketch, "E31.0.112", {"start": v(23.83, -9.72) * mm, "mid": v(25.55, -9.43) * mm, "end": v(27.12, -8.68) * mm});
            skArc(sketch, "E31.0.113", {"start": v(27.12, -8.68) * mm, "mid": v(27.23, -8.58) * mm, "end": v(27.31, -8.45) * mm});
            skLineSegment(sketch, "E31.0.114", {"start": v(27.31, -8.45) * mm, "end": v(27.37, -8.3) * mm});
            skLineSegment(sketch, "E31.0.115", {"start": v(27.37, -8.3) * mm, "end": v(27.4, -8.15) * mm});
            skArc(sketch, "E31.0.116", {"start": v(27.4, -8.15) * mm, "mid": v(27.41, -8) * mm, "end": v(27.37, -7.85) * mm});
            skArc(sketch, "E31.0.117", {"start": v(27.37, -7.85) * mm, "mid": v(26.48, -6.35) * mm, "end": v(25.22, -5.15) * mm});
            skArc(sketch, "E31.0.118", {"start": v(25.22, -5.15) * mm, "mid": v(24.92, -4.99) * mm, "end": v(24.6, -4.89) * mm});
            skLineSegment(sketch, "E31.0.119", {"start": v(24.6, -4.89) * mm, "end": v(23.3, -4.63) * mm});
            skArc(sketch, "E31.0.120", {"start": v(23.3, -4.63) * mm, "mid": v(22.32, -4) * mm, "end": v(22.04, -2.87) * mm});
            skArc(sketch, "E31.0.121", {"start": v(22.04, -2.87) * mm, "mid": v(22.12, -2.18) * mm, "end": v(22.18, -1.49) * mm});
            skArc(sketch, "E31.0.122", {"start": v(22.18, -1.49) * mm, "mid": v(22.67, -0.43) * mm, "end": v(23.76, 0) * mm});
            skLineSegment(sketch, "E31.0.123", {"start": v(23.76, 0) * mm, "end": v(25.08, 0) * mm});
            skArc(sketch, "E31.0.124", {"start": v(25.08, 0) * mm, "mid": v(25.42, 0.03) * mm, "end": v(25.74, 0.14) * mm});
            skArc(sketch, "E31.0.125", {"start": v(25.74, 0.14) * mm, "mid": v(27.21, 1.06) * mm, "end": v(28.38, 2.36) * mm});
            skArc(sketch, "E31.0.126", {"start": v(28.38, 2.36) * mm, "mid": v(28.44, 2.5) * mm, "end": v(28.47, 2.64) * mm});
            skLineSegment(sketch, "E31.0.127", {"start": v(28.47, 2.64) * mm, "end": v(28.47, 2.8) * mm});
            skLineSegment(sketch, "E31.0.128", {"start": v(28.47, 2.8) * mm, "end": v(28.44, 2.96) * mm});
            skArc(sketch, "E31.0.129", {"start": v(28.44, 2.96) * mm, "mid": v(28.38, 3.1) * mm, "end": v(28.3, 3.22) * mm});
            skArc(sketch, "E31.0.130", {"start": v(28.3, 3.22) * mm, "mid": v(26.9, 4.27) * mm, "end": v(25.27, 4.89) * mm});
            skArc(sketch, "E31.0.131", {"start": v(25.27, 4.89) * mm, "mid": v(24.94, 4.93) * mm, "end": v(24.6, 4.9) * mm});
            skLineSegment(sketch, "E31.0.132", {"start": v(24.6, 4.9) * mm, "end": v(23.3, 4.64) * mm});
            skArc(sketch, "E31.0.133", {"start": v(23.3, 4.64) * mm, "mid": v(22.15, 4.85) * mm, "end": v(21.46, 5.78) * mm});
            skArc(sketch, "E31.0.134", {"start": v(21.46, 5.78) * mm, "mid": v(21.27, 6.45) * mm, "end": v(21.06, 7.11) * mm});
            skArc(sketch, "E31.0.135", {"start": v(21.06, 7.11) * mm, "mid": v(21.11, 8.28) * mm, "end": v(21.95, 9.09) * mm});
            skLineSegment(sketch, "E31.0.136", {"start": v(21.95, 9.09) * mm, "end": v(23.18, 9.6) * mm});
            skArc(sketch, "E31.0.137", {"start": v(23.18, 9.6) * mm, "mid": v(23.47, 9.75) * mm, "end": v(23.73, 9.97) * mm});
            skArc(sketch, "E31.0.138", {"start": v(23.73, 9.97) * mm, "mid": v(24.73, 11.4) * mm, "end": v(25.32, 13.04) * mm});
            skArc(sketch, "E31.0.139", {"start": v(25.32, 13.04) * mm, "mid": v(25.32, 13.2) * mm, "end": v(25.29, 13.34) * mm});
            skLineSegment(sketch, "E31.0.140", {"start": v(25.29, 13.34) * mm, "end": v(25.23, 13.48) * mm});
            skLineSegment(sketch, "E31.0.141", {"start": v(25.23, 13.48) * mm, "end": v(25.14, 13.62) * mm});
            skArc(sketch, "E31.0.142", {"start": v(25.14, 13.62) * mm, "mid": v(25.04, 13.73) * mm, "end": v(24.9, 13.8) * mm});
            skArc(sketch, "E31.0.143", {"start": v(24.9, 13.8) * mm, "mid": v(23.22, 14.23) * mm, "end": v(21.47, 14.19) * mm});
            skArc(sketch, "E31.0.144", {"start": v(21.47, 14.19) * mm, "mid": v(21.15, 14.1) * mm, "end": v(20.85, 13.94) * mm});
            skLineSegment(sketch, "E31.0.145", {"start": v(20.85, 13.94) * mm, "end": v(19.75, 13.2) * mm});
            skArc(sketch, "E31.0.146", {"start": v(19.75, 13.2) * mm, "mid": v(18.61, 12.96) * mm, "end": v(17.61, 13.56) * mm});
            skArc(sketch, "E31.0.147", {"start": v(17.61, 13.56) * mm, "mid": v(17.18, 14.1) * mm, "end": v(16.73, 14.63) * mm});
            skArc(sketch, "E31.0.148", {"start": v(16.73, 14.63) * mm, "mid": v(16.34, 15.73) * mm, "end": v(16.8, 16.8) * mm});
            skLineSegment(sketch, "E31.0.149", {"start": v(16.8, 16.8) * mm, "end": v(17.74, 17.73) * mm});
            skArc(sketch, "E31.0.150", {"start": v(17.74, 17.73) * mm, "mid": v(17.95, 18) * mm, "end": v(18.1, 18.3) * mm});
            skArc(sketch, "E31.0.151", {"start": v(18.1, 18.3) * mm, "mid": v(18.49, 20) * mm, "end": v(18.4, 21.74) * mm});
            skArc(sketch, "E31.0.152", {"start": v(18.4, 21.74) * mm, "mid": v(18.35, 21.88) * mm, "end": v(18.26, 22) * mm});
            skLineSegment(sketch, "E31.0.153", {"start": v(18.26, 22) * mm, "end": v(18.15, 22.11) * mm});
            skLineSegment(sketch, "E31.0.154", {"start": v(18.15, 22.11) * mm, "end": v(18.01, 22.2) * mm});
            skArc(sketch, "E31.0.155", {"start": v(18.01, 22.2) * mm, "mid": v(17.88, 22.26) * mm, "end": v(17.73, 22.29) * mm});
            skArc(sketch, "E31.0.156", {"start": v(17.73, 22.29) * mm, "mid": v(16, 22.03) * mm, "end": v(14.41, 21.32) * mm});
            skArc(sketch, "E31.0.157", {"start": v(14.41, 21.32) * mm, "mid": v(14.15, 21.12) * mm, "end": v(13.93, 20.86) * mm});
            skLineSegment(sketch, "E31.0.158", {"start": v(13.93, 20.86) * mm, "end": v(13.2, 19.76) * mm});
            skArc(sketch, "E31.0.159", {"start": v(13.2, 19.76) * mm, "mid": v(12.24, 19.1) * mm, "end": v(11.08, 19.26) * mm});
            skArc(sketch, "E31.0.160", {"start": v(11.08, 19.26) * mm, "mid": v(10.48, 19.6) * mm, "end": v(9.86, 19.92) * mm});
            skArc(sketch, "E31.0.161", {"start": v(9.86, 19.92) * mm, "mid": v(9.08, 20.78) * mm, "end": v(9.1, 21.95) * mm});
            skLineSegment(sketch, "E31.0.162", {"start": v(9.1, 21.95) * mm, "end": v(9.6, 23.17) * mm});
            skArc(sketch, "E31.0.163", {"start": v(9.6, 23.17) * mm, "mid": v(9.7, 23.5) * mm, "end": v(9.72, 23.83) * mm});
            skArc(sketch, "E31.0.164", {"start": v(9.72, 23.83) * mm, "mid": v(9.43, 25.55) * mm, "end": v(8.68, 27.12) * mm});
            skArc(sketch, "E31.0.165", {"start": v(8.68, 27.12) * mm, "mid": v(8.58, 27.23) * mm, "end": v(8.45, 27.31) * mm});
            skLineSegment(sketch, "E31.0.166", {"start": v(8.45, 27.31) * mm, "end": v(8.3, 27.37) * mm});
            skLineSegment(sketch, "E31.0.167", {"start": v(8.3, 27.37) * mm, "end": v(8.15, 27.4) * mm});
            skArc(sketch, "E31.0.168", {"start": v(8.15, 27.4) * mm, "mid": v(8, 27.41) * mm, "end": v(7.85, 27.37) * mm});
            skArc(sketch, "E31.0.169", {"start": v(7.85, 27.37) * mm, "mid": v(6.35, 26.48) * mm, "end": v(5.15, 25.22) * mm});
            skArc(sketch, "E31.0.170", {"start": v(5.15, 25.22) * mm, "mid": v(4.99, 24.92) * mm, "end": v(4.89, 24.6) * mm});
            skLineSegment(sketch, "E31.0.171", {"start": v(4.89, 24.6) * mm, "end": v(4.63, 23.3) * mm});
            skArc(sketch, "E31.0.172", {"start": v(4.63, 23.3) * mm, "mid": v(4, 22.32) * mm, "end": v(2.87, 22.04) * mm});
            skArc(sketch, "E31.0.173", {"start": v(2.87, 22.04) * mm, "mid": v(2.18, 22.12) * mm, "end": v(1.49, 22.18) * mm});
            skArc(sketch, "E31.0.174", {"start": v(1.49, 22.18) * mm, "mid": v(0.43, 22.67) * mm, "end": v(0, 23.76) * mm});
            skLineSegment(sketch, "E31.0.175", {"start": v(0, 23.76) * mm, "end": v(0, 25.08) * mm});
            skArc(sketch, "E31.0.176", {"start": v(0, 25.08) * mm, "mid": v(-0.03, 25.42) * mm, "end": v(-0.14, 25.74) * mm});
            skArc(sketch, "E31.0.177", {"start": v(-0.14, 25.74) * mm, "mid": v(-1.06, 27.21) * mm, "end": v(-2.36, 28.38) * mm});
            skArc(sketch, "E31.0.178", {"start": v(-2.36, 28.38) * mm, "mid": v(-2.5, 28.44) * mm, "end": v(-2.64, 28.47) * mm});
            skLineSegment(sketch, "E31.0.179", {"start": v(-2.64, 28.47) * mm, "end": v(-2.8, 28.47) * mm});
            skLineSegment(sketch, "E31.0.180", {"start": v(-2.8, 28.47) * mm, "end": v(-2.96, 28.44) * mm});
            skArc(sketch, "E31.0.181", {"start": v(-2.96, 28.44) * mm, "mid": v(-3.1, 28.38) * mm, "end": v(-3.22, 28.3) * mm});
            skArc(sketch, "E31.0.182", {"start": v(-3.22, 28.3) * mm, "mid": v(-4.27, 26.9) * mm, "end": v(-4.89, 25.27) * mm});
            skArc(sketch, "E31.0.183", {"start": v(-4.89, 25.27) * mm, "mid": v(-4.93, 24.94) * mm, "end": v(-4.9, 24.6) * mm});
            skLineSegment(sketch, "E31.0.184", {"start": v(-4.9, 24.6) * mm, "end": v(-4.64, 23.3) * mm});
            skArc(sketch, "E31.0.185", {"start": v(-4.64, 23.3) * mm, "mid": v(-4.85, 22.15) * mm, "end": v(-5.78, 21.46) * mm});
            skArc(sketch, "E31.0.186", {"start": v(-5.78, 21.46) * mm, "mid": v(-6.45, 21.27) * mm, "end": v(-7.11, 21.06) * mm});
            skArc(sketch, "E31.0.187", {"start": v(-7.11, 21.06) * mm, "mid": v(-8.28, 21.11) * mm, "end": v(-9.09, 21.95) * mm});
            skLineSegment(sketch, "E31.0.188", {"start": v(-9.09, 21.95) * mm, "end": v(-9.6, 23.18) * mm});
            skArc(sketch, "E31.0.189", {"start": v(-9.6, 23.18) * mm, "mid": v(-9.75, 23.47) * mm, "end": v(-9.97, 23.73) * mm});
            skArc(sketch, "E31.0.190", {"start": v(-9.97, 23.73) * mm, "mid": v(-11.4, 24.73) * mm, "end": v(-13.04, 25.32) * mm});
            skArc(sketch, "E31.0.191", {"start": v(-13.04, 25.32) * mm, "mid": v(-13.2, 25.32) * mm, "end": v(-13.34, 25.29) * mm});
            skLineSegment(sketch, "E31.0.192", {"start": v(-13.34, 25.29) * mm, "end": v(-13.48, 25.23) * mm});
            skLineSegment(sketch, "E31.0.193", {"start": v(-13.48, 25.23) * mm, "end": v(-13.62, 25.14) * mm});
            skArc(sketch, "E31.0.194", {"start": v(-13.62, 25.14) * mm, "mid": v(-13.73, 25.04) * mm, "end": v(-13.8, 24.9) * mm});
            skArc(sketch, "E31.0.195", {"start": v(-13.8, 24.9) * mm, "mid": v(-14.23, 23.22) * mm, "end": v(-14.19, 21.47) * mm});
            skArc(sketch, "E31.0.196", {"start": v(-14.19, 21.47) * mm, "mid": v(-14.1, 21.15) * mm, "end": v(-13.94, 20.85) * mm});
            skLineSegment(sketch, "E31.0.197", {"start": v(-13.94, 20.85) * mm, "end": v(-13.2, 19.75) * mm});
            skArc(sketch, "E31.0.198", {"start": v(-13.2, 19.75) * mm, "mid": v(-12.96, 18.61) * mm, "end": v(-13.56, 17.61) * mm});
            skArc(sketch, "E31.0.199", {"start": v(-13.56, 17.61) * mm, "mid": v(-14.1, 17.18) * mm, "end": v(-14.63, 16.73) * mm});
            skArc(sketch, "E31.0.200", {"start": v(-14.63, 16.73) * mm, "mid": v(-15.73, 16.34) * mm, "end": v(-16.8, 16.8) * mm});
            skLineSegment(sketch, "E31.0.201", {"start": v(-16.8, 16.8) * mm, "end": v(-17.73, 17.74) * mm});
            skArc(sketch, "E31.0.202", {"start": v(-17.73, 17.74) * mm, "mid": v(-18, 17.95) * mm, "end": v(-18.3, 18.1) * mm});
            skArc(sketch, "E31.0.203", {"start": v(-18.3, 18.1) * mm, "mid": v(-20, 18.49) * mm, "end": v(-21.74, 18.4) * mm});
            skArc(sketch, "E31.0.204", {"start": v(-21.74, 18.4) * mm, "mid": v(-21.88, 18.35) * mm, "end": v(-22, 18.26) * mm});
            skLineSegment(sketch, "E31.0.205", {"start": v(-22, 18.26) * mm, "end": v(-22.11, 18.15) * mm});
            skLineSegment(sketch, "E31.0.206", {"start": v(-22.11, 18.15) * mm, "end": v(-22.2, 18.01) * mm});
            skArc(sketch, "E31.0.207", {"start": v(-22.2, 18.01) * mm, "mid": v(-22.26, 17.88) * mm, "end": v(-22.29, 17.73) * mm});
            skSolve(sketch);
        }
        {
            var Q0;
            Q0=makeQuery(id+"F0.imprint","IMPRINT",FACE,{"disambiguationData":[TD([[makeQuery(id+"F0.imprint","IMPRINT",EDGE,{"derivedFrom":sQuery(id+"F0.wireOp",EDGE,"E0")}),1.0]])]});
            var Q1;
            Q1=makeQuery(id+"F2.imprint","IMPRINT",FACE,{"disambiguationData":[TD([[makeQuery(id+"F2.imprint","IMPRINT",EDGE,{"derivedFrom":sQuery(id+"F2.wireOp",EDGE,"E31.0.0")}),1.0]])]});
            var Q2;
            Q2=sQuery(id+"F2.wireOp",VERTEX,"E31.0.197.start");
            var Q3;
            Q3=sQuery(id+"F0.wireOp",VERTEX,"E6.MirrorCS.start");
            loft(context, id + "F3", {"sheetProfilesArray" : [{ "sheetProfileEntities" : qUnion([Q0]) }, { "sheetProfileEntities" : qUnion([Q1]) }], "matchConnections" : true, "connections" : [{ "connectionEntities" : qUnion([Q2, Q3]), "connectionEdgeQueries" : qUnion([]), "connectionEdgeParameters" : [] }]});
        }
        {
            var Q0;
            Q0=makeQuery(id+"F3.opLoft","CAP_FACE",FACE,{"disambiguationData":[OSD([makeQuery(id+"F2.imprint","IMPRINT",FACE,{"disambiguationData":[TD([[makeQuery(id+"F2.imprint","IMPRINT",EDGE,{"derivedFrom":sQuery(id+"F2.wireOp",EDGE,"E31.0.0")}),1.0]])]})])],"isStart":true});
            var sketch = newSketch(context, id + "F4", { "sketchPlane" : qUnion([Q0])});
            skPoint(sketch, "E32", {"position": v(0, 0) * mm});
            skSolve(sketch);
        }
        {
            var Q0;
            Q0=sQuery(id+"F4.wireOp",VERTEX,"E32");
            var Q1;
            Q1=makeQuery(id+"F3.opLoft","SWEPT_BODY",BODY,{"disambiguationData":[OSD([makeQuery(id+"F0.imprint","IMPRINT",FACE,{"disambiguationData":[TD([[makeQuery(id+"F0.imprint","IMPRINT",EDGE,{"derivedFrom":sQuery(id+"F0.wireOp",EDGE,"E0")}),1.0]])]}),makeQuery(id+"F2.imprint","IMPRINT",FACE,{"disambiguationData":[TD([[makeQuery(id+"F2.imprint","IMPRINT",EDGE,{"derivedFrom":sQuery(id+"F2.wireOp",EDGE,"E31.0.0")}),1.0]])]})])]});
            hole(context, id + "F5", {"style" : HoleStyle.SIMPLE, "endStyle" : HoleEndStyle.THROUGH, "holeDiameter" : 12.7 * mm, "tappedDepth" : 12.7 * mm, "tapClearance" : 3, "locations" : qUnion([Q0]), "scope" : qUnion([Q1])});
        }
    });
